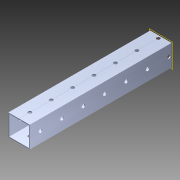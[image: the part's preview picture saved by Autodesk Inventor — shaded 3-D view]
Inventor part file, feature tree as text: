
AUTODESK INVENTOR PART (.ipt)
format: ipt  version: 2014 SP1 (Build 180222100, 222)  size: 1,142,272 bytes
history: native  units: in
note: dims shown in document units (in); Inventor stores cm internally (conversion verified against a paired STEP export)
features: pattern_circular x1, other x1, plane x1, extrude x1, imported_body x1, sketch x1
ambient origin geometry x8: Origin, YZ Plane, XZ Plane, XY Plane, X Axis, Y Axis, Z Axis, Center Point
bodies: Body1 (feature_tree)
feature tree (6):
  pattern_circular  "CirPattern2"
  other  "217-3426-STEP1"
  plane  "Work Plane1"
  extrude  "Extrusion1"  Depth=3937.0079in TaperAngle=0.0deg
  imported_body  "Base1"
  sketch  "Sketch1"  dims[d0=-6.625in d1=3937.0079in d2=0.0in]
